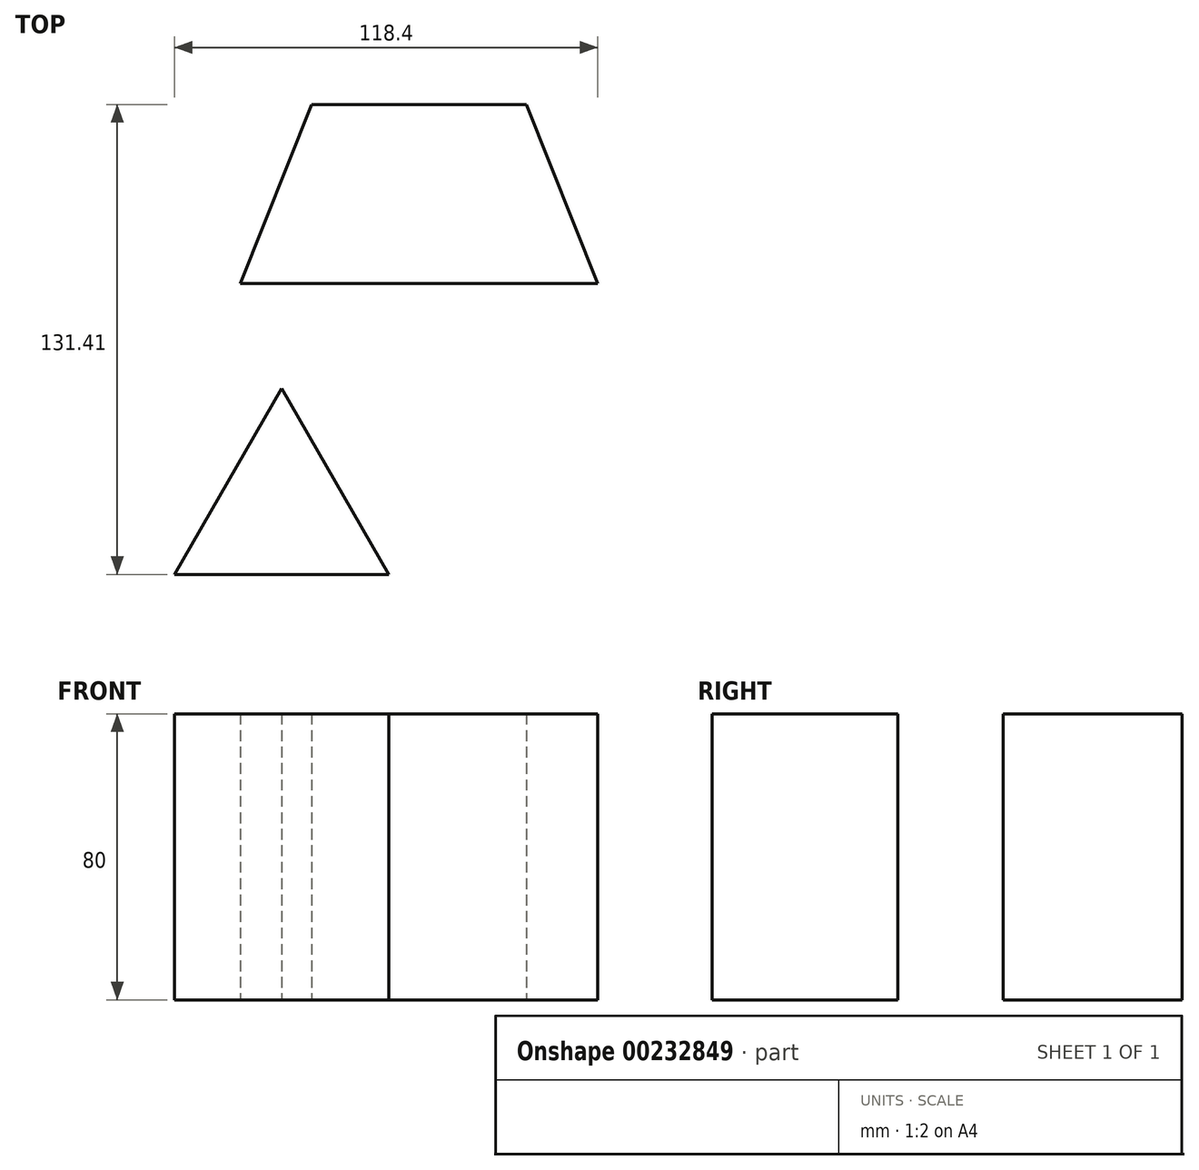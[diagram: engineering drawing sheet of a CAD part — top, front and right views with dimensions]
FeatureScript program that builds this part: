
annotation { "Feature Type Name" : "Feature", "Feature Type Description" : "" }
export const myFeature = defineFeature(function(context is Context, id is Id, definition is map)
    precondition{}
    {
        {
            var Q0;
            Q0=qCreatedBy(makeId("Top.planeOp"),FACE);
            var sketch = newSketch(context, id + "F0", { "sketchPlane" : qUnion([Q0])});
            skLineSegment(sketch, "E0", {"start": v(-110.5, 23.76) * mm, "end": v(-30.5, 23.76) * mm});
            skLineSegment(sketch, "E1", {"start": v(-30.5, 23.76) * mm, "end": v(-0.5, 75.72) * mm});
            skLineSegment(sketch, "E2", {"start": v(-110.5, 23.76) * mm, "end": v(-86.56, 89.54) * mm});
            skLineSegment(sketch, "E3", {"start": v(-86.56, 89.54) * mm, "end": v(-45.87, 89.54) * mm});
            skLineSegment(sketch, "E4", {"start": v(-86.56, 89.54) * mm, "end": v(-61.84, 76.39) * mm});
            skLineSegment(sketch, "E5", {"start": v(-21.94, -16.27) * mm, "end": v(-51.94, -68.23) * mm});
            skLineSegment(sketch, "E6", {"start": v(-51.94, -68.23) * mm, "end": v(8.06, -68.23) * mm});
            skLineSegment(sketch, "E7", {"start": v(8.06, -68.23) * mm, "end": v(-21.94, -16.27) * mm});
            skLineSegment(sketch, "E8", {"start": v(-33.54, 13.18) * mm, "end": v(66.46, 13.18) * mm});
            skLineSegment(sketch, "E9", {"start": v(66.46, 13.18) * mm, "end": v(46.46, 63.18) * mm});
            skLineSegment(sketch, "E10", {"start": v(46.46, 63.18) * mm, "end": v(-13.54, 63.18) * mm});
            skLineSegment(sketch, "E11", {"start": v(-13.54, 63.18) * mm, "end": v(-33.54, 13.18) * mm});
            skSolve(sketch);
        }
        {
            var Q0;
            Q0 = qSketchRegion(id + "F0", true);
            extrude(context, id + "F1", {"entities" : qUnion([Q0]), "depth" : 80 * mm});
        }
    });
